# Revit family: elupura s wc seat and cover with top fix, softclose and quickrelease, slim
name_source: partatom
category: Plumbing Fixtures
units: mm (PartAtom-declared; Revit-internal decimal feet)

## family parameters
Always vertical = Yes
Cut with Voids When Loaded = No
OmniClass Number = 23.45.00.00
OmniClass Title = Sanitary, Laundry, and Cleaning Equipment
Part Type = Normal
Room Calculation Point = No
Round Connector Dimension = Use Diameter
Shared = Yes
Work Plane-Based = No

## types (2) — shared parameters
ARTNR = 60200450
BASENUMBER = 60200
BIMOBJECT = Sanitary: Toilet Seats
CATALOG = Hansgrohe
COLLECTION = toilet seats
COLLECTIONSET = EluPura S
DEPTH = 440
DESIGN = Germany
GTINCODE = 4059625420966
IDNR = 1
IFC = Furnishing element
Manufacturer = Hansgrohe
NAME = EluPura S WC seat and cover with top fix, SoftClose and QuickRelease, Slim
NBSYN = $BASENUMBER.-$ARTNR.-$SURFACE.-$LODLEVEL.
NN = EluPura S WC seat and cover with top fix, SoftClose and QuickRelease, Slim
OBJECTTYPE = Object (single object)
OMNICLASS = 23-31 19 00 | Toilets
PERMALINK = 60200XXX
PRODUCTURL = https://pro.hansgrohe.com
REGION = Worldwide
SPECIFICATION = Surfaces:  - 60200450 White   Specification:  • consists of: WC seat, cover  • material: Urea  • degree of gloss: glossy  • with comfortable SoftClose mechanism • QuickRelease: quick removable toilet seat and cover
SURFACE = GLOSSY_WHITE
UNICLASS2015 = Pr_40_20_93_95 | WC seats and covers
UNICLASS_2015_CODE = 40_20_93_95
WEIGHT = 4.6
WIDTH = 366
zero-valued in all types: HEIGHT

## per-type parameters (varying)
| type | LODLEVEL |
| 60200-60200450-GLOSSY_WHITE-200 | 200 |
| 60200-60200450-GLOSSY_WHITE-400 | 400 |

note: column(s) folded — value = type name in every type: LINA, Model, NB

type visibility flags: 2 boolean params named "<type name>_RX0RY0RZ0TX0TY0TZ0_V" — each type sets only its own to Yes (folded from table)

## geometry (parser evidence)
native form markers: Sweep x23
no freeform markers — native parametric forms only
